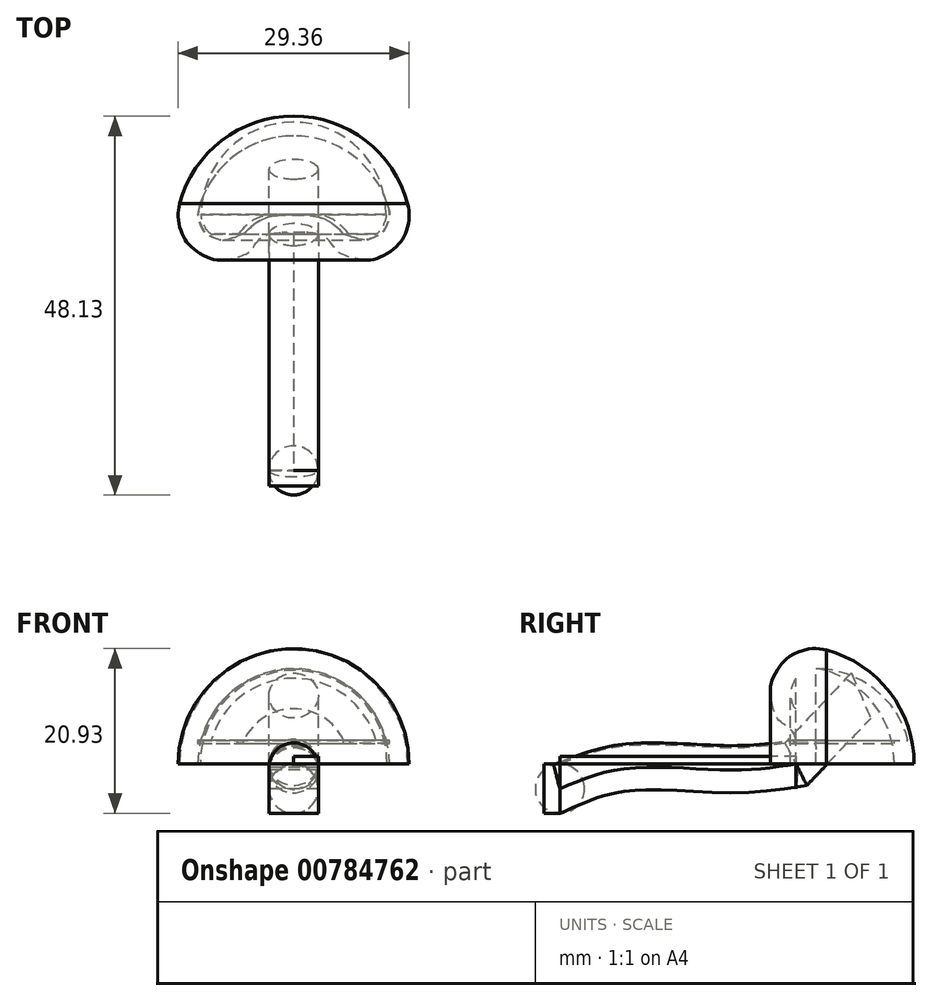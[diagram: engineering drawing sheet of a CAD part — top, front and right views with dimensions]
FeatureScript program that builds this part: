
annotation { "Feature Type Name" : "Feature", "Feature Type Description" : "" }
export const myFeature = defineFeature(function(context is Context, id is Id, definition is map)
    precondition{}
    {
        {
            var Q0;
            Q0=qCreatedBy(makeId("Top.planeOp"),FACE);
            var sketch = newSketch(context, id + "F0", { "sketchPlane" : qUnion([Q0])});
            skArc(sketch, "E0", {"start": v(14.49, 3.88) * mm, "mid": v(0, 15) * mm, "end": v(-14.49, 3.88) * mm});
            skFitSpline(sketch, "E1", {"points": [v(-14.49, 3.88) * mm, v(-14.67, 2.02) * mm, v(-14.1, -0.07) * mm, v(-13.11, -1.5) * mm, v(-10.97, -2.91) * mm, v(-8.92, -3.26) * mm, v(-6.48, -2.67) * mm, v(-5.4, -1.97) * mm, v(-4.1, -0.42) * mm, v(-2.07, 0.17) * mm, v(-1.02, 0.18) * mm, v(0, 0) * mm], "startDerivative": vector(-3.74, -19.6) * mm, "endDerivative": vector(15.18, -3.15) * mm});
            skFitSpline(sketch, "E2.MirrorCS", {"points": [v(14.49, 3.88) * mm, v(14.67, 2.02) * mm, v(14.1, -0.07) * mm, v(13.11, -1.5) * mm, v(10.97, -2.91) * mm, v(8.92, -3.26) * mm, v(6.48, -2.67) * mm, v(5.4, -1.97) * mm, v(4.1, -0.42) * mm, v(2.07, 0.17) * mm, v(1.02, 0.18) * mm, v(0, 0) * mm], "startDerivative": vector(3.74, -19.6) * mm, "endDerivative": vector(-15.18, -3.15) * mm});
            skLineSegment(sketch, "E3.trimOffspring", {"start": v(-3.13, 0) * mm, "end": v(3.13, 0) * mm});
            skLineSegment(sketch, "E4", {"start": v(0, 15) * mm, "end": v(0, 0) * mm});
            skSolve(sketch);
        }
        {
            var Q0;
            {var subQ0=sQuery(id+"F0.wireOp",EDGE,"E3.trimOffspring");var subQ1=sQuery(id+"F0.wireOp",EDGE,"E1");var subQ3=makeQuery(id+"F0.imprint","INTERSECT",VERTEX,{"derivedFrom":[subQ1,subQ0]});Q0=makeQuery(id+"F0.imprint","IMPRINT",FACE,{"disambiguationData":[TD([[makeQuery(id+"F0.imprint","IMPRINT",EDGE,{"disambiguationData":[TD([[subQ3,-1.0]])],"derivedFrom":subQ1}),-1.0]])]});}
            var Q1;
            {var subQ0=sQuery(id+"F0.wireOp",EDGE,"E3.trimOffspring");var subQ1=sQuery(id+"F0.wireOp",EDGE,"E2.MirrorCS");var subQ3=makeQuery(id+"F0.imprint","INTERSECT",VERTEX,{"derivedFrom":[subQ1,subQ0]});Q1=makeQuery(id+"F0.imprint","IMPRINT",FACE,{"disambiguationData":[TD([[makeQuery(id+"F0.imprint","IMPRINT",EDGE,{"disambiguationData":[TD([[subQ3,-1.0]])],"derivedFrom":subQ1}),1.0]])]});}
            var Q2;
            {var subQ3=sQuery(id+"F0.wireOp",EDGE,"E4");Q2=makeQuery(id+"F0.imprint","IMPRINT",FACE,{"disambiguationData":[TD([[makeQuery(id+"F0.imprint","IMPRINT",EDGE,{"derivedFrom":subQ3}),1.0]])]});}
            var Q3;
            Q3=sQuery(id+"F0.wireOp",EDGE,"E4");
            revolve(context, id + "F1", {"entities" : qUnion([Q0, Q1, Q2]), "axis" : qUnion([Q3]), "revolveType" : RevolveType.ONE_DIRECTION, "angle" : 180 * degree});
        }
        {
            var Q0;
            Q0=makeQuery(id+"F1.opRevolve","CAP_FACE",FACE,{"disambiguationData":[OSD([sQuery(id+"F0.wireOp",EDGE,"E0"),sQuery(id+"F0.wireOp",EDGE,"E2.MirrorCS"),sQuery(id+"F0.wireOp",EDGE,"E3.trimOffspring"),sQuery(id+"F0.wireOp",EDGE,"E4")])],"isStart":false});
            var sketch = newSketch(context, id + "F2", { "sketchPlane" : qUnion([Q0])});
            skArc(sketch, "E5", {"start": v(-11.88, -3.88) * mm, "mid": v(0, -12.5) * mm, "end": v(11.88, -3.88) * mm});
            skLineSegment(sketch, "E6", {"start": v(14.49, -3.88) * mm, "end": v(14.68, -2.52) * mm, "construction": true});
            skLineSegment(sketch, "E7", {"start": v(14.68, -2.52) * mm, "end": v(14.3, -0.42) * mm, "construction": true});
            skLineSegment(sketch, "E8", {"start": v(14.3, -0.42) * mm, "end": v(13.11, 1.5) * mm, "construction": true});
            skLineSegment(sketch, "E9", {"start": v(13.11, 1.5) * mm, "end": v(11.35, 2.73) * mm, "construction": true});
            skLineSegment(sketch, "E10", {"start": v(11.35, 2.73) * mm, "end": v(9.25, 3.27) * mm, "construction": true});
            skLineSegment(sketch, "E11", {"start": v(9.25, 3.27) * mm, "end": v(7.87, 3.09) * mm, "construction": true});
            skLineSegment(sketch, "E12", {"start": v(7.87, 3.09) * mm, "end": v(6.48, 2.67) * mm, "construction": true});
            skLineSegment(sketch, "E13", {"start": v(6.48, 2.67) * mm, "end": v(5.56, 2.13) * mm, "construction": true});
            skLineSegment(sketch, "E14", {"start": v(3.13, 0) * mm, "end": v(4.1, 0.43) * mm});
            skLineSegment(sketch, "E15", {"start": v(4.1, 0.43) * mm, "end": v(3.13, 0) * mm, "construction": true});
            skLineSegment(sketch, "E16", {"start": v(14.58, -3.2) * mm, "end": v(12.1, -2.86) * mm, "construction": true});
            skLineSegment(sketch, "E17", {"start": v(14.5, -1.47) * mm, "end": v(12.03, -1.9) * mm, "construction": true});
            skLineSegment(sketch, "E18", {"start": v(13.71, 0.54) * mm, "end": v(11.49, -0.6) * mm, "construction": true});
            skLineSegment(sketch, "E19", {"start": v(12.23, 2.12) * mm, "end": v(10.8, 0.07) * mm, "construction": true});
            skLineSegment(sketch, "E20", {"start": v(10.3, 3) * mm, "end": v(9.67, 0.58) * mm, "construction": true});
            skLineSegment(sketch, "E21", {"start": v(8.56, 3.18) * mm, "end": v(8.9, 0.7) * mm, "construction": true});
            skLineSegment(sketch, "E22", {"start": v(7.18, 2.88) * mm, "end": v(7.9, 0.49) * mm, "construction": true});
            skLineSegment(sketch, "E23", {"start": v(6.02, 2.4) * mm, "end": v(7.27, 0.24) * mm, "construction": true});
            skLineSegment(sketch, "E24", {"start": v(4.1, 0.43) * mm, "end": v(5.56, 2.13) * mm, "construction": true});
            skLineSegment(sketch, "E25", {"start": v(4.83, 1.28) * mm, "end": v(6.73, -0.34) * mm, "construction": true});
            skLineSegment(sketch, "E26", {"start": v(3.62, 0.22) * mm, "end": v(4.62, -2.07) * mm, "construction": true});
            skLineSegment(sketch, "E27", {"start": v(3.13, 0) * mm, "end": v(0, 0) * mm, "construction": true});
            skLineSegment(sketch, "E28", {"start": v(1.56, 0) * mm, "end": v(1.56, -2.5) * mm, "construction": true});
            skFitSpline(sketch, "E29", {"points": [v(11.88, -3.88) * mm, v(12.1, -2.86) * mm, v(12.03, -1.9) * mm, v(11.49, -0.6) * mm, v(10.8, 0.07) * mm, v(9.67, 0.58) * mm, v(8.9, 0.7) * mm, v(7.9, 0.49) * mm, v(7.27, 0.24) * mm, v(6.73, -0.34) * mm, v(4.62, -2.07) * mm, v(1.56, -2.5) * mm, v(0, -2.5) * mm], "startDerivative": vector(3.76, 13.81) * mm, "endDerivative": vector(-15.24, -0.04) * mm});
            skFitSpline(sketch, "E30.MirrorCS", {"points": [v(-11.88, -3.88) * mm, v(-12.1, -2.86) * mm, v(-12.03, -1.9) * mm, v(-11.49, -0.6) * mm, v(-10.8, 0.07) * mm, v(-9.67, 0.58) * mm, v(-8.9, 0.7) * mm, v(-7.9, 0.49) * mm, v(-7.27, 0.24) * mm, v(-6.73, -0.34) * mm, v(-4.62, -2.07) * mm, v(-1.56, -2.5) * mm, v(0, -2.5) * mm], "startDerivative": vector(-3.76, 13.81) * mm, "endDerivative": vector(15.24, -0.04) * mm});
            skLineSegment(sketch, "E31", {"start": v(0, -12.5) * mm, "end": v(0, -2.5) * mm});
            skSolve(sketch);
        }
        {
            var Q0;
            {var subQ0=sQuery(id+"F2.wireOp",EDGE,"E29");Q0=makeQuery(id+"F2.imprint","IMPRINT",FACE,{"disambiguationData":[TD([[makeQuery(id+"F2.imprint","IMPRINT",EDGE,{"derivedFrom":subQ0}),1.0]])]});}
            var Q1;
            Q1=sQuery(id+"F2.wireOp",EDGE,"E31");
            revolve(context, id + "F3", {"operationType" : NewBodyOperationType.REMOVE, "entities" : qUnion([Q0]), "axis" : qUnion([Q1]), "revolveType" : RevolveType.ONE_DIRECTION, "angle" : 180 * degree});
        }
        {
            var Q0;
            Q0=qCreatedBy(makeId("Front.planeOp"),FACE);
            var sketch = newSketch(context, id + "F4", { "sketchPlane" : qUnion([Q0])});
            skLineSegment(sketch, "E32", {"start": v(0, 0) * mm, "end": v(0, 3) * mm});
            skArc(sketch, "E33", {"start": v(14.14, 0) * mm, "mid": v(0, 14.14) * mm, "end": v(-14.14, 0) * mm});
            skLineSegment(sketch, "E34", {"start": v(0, 3) * mm, "end": v(-13.82, 3) * mm});
            skLineSegment(sketch, "E35", {"start": v(-13.82, 3) * mm, "end": v(13.82, 3) * mm});
            skLineSegment(sketch, "E36.bottom", {"start": v(-13.82, 3) * mm, "end": v(12.58, 3) * mm});
            skLineSegment(sketch, "E36.left", {"start": v(-13.82, 3) * mm, "end": v(-13.82, 3.47) * mm});
            skLineSegment(sketch, "E36.right", {"start": v(12.58, 3) * mm, "end": v(12.58, 6.47) * mm});
            skLineSegment(sketch, "E37.left", {"start": v(-13.82, 3.47) * mm, "end": v(-13.82, 3) * mm});
            skLineSegment(sketch, "E37.right", {"start": v(13.82, 3.47) * mm, "end": v(13.82, 3) * mm});
            skLineSegment(sketch, "E38.bottom", {"start": v(-0.5, 3) * mm, "end": v(1.98, 3) * mm});
            skSolve(sketch);
        }
        {
            var Q0;
            {var subQ2=sQuery(id+"F4.wireOp",EDGE,"E36.right");Q0=makeQuery(id+"F4.imprint","IMPRINT",FACE,{"disambiguationData":[TD([[makeQuery(id+"F4.imprint","IMPRINT",EDGE,{"derivedFrom":subQ2}),1.0]])]});}
            extrude(context, id + "F5", {"entities" : qUnion([Q0]), "operationType" : NewBodyOperationType.ADD, "oppositeDirection" : true, "depth" : 2.5 * mm, "offsetDistance" : 25 * mm});
        }
        {
            var Q0;
            Q0=makeQuery(id+"F5.opExtrude","CAP_FACE",FACE,{"disambiguationData":[OSD([sQuery(id+"F4.wireOp",EDGE,"E33"),sQuery(id+"F4.wireOp",EDGE,"E34"),sQuery(id+"F4.wireOp",EDGE,"E35"),sQuery(id+"F4.wireOp",EDGE,"E36.right")])],"isStart":false});
            var sketch = newSketch(context, id + "F6", { "sketchPlane" : qUnion([Q0])});
            skLineSegment(sketch, "E39", {"start": v(0, 3) * mm, "end": v(0, 12.12) * mm});
            skSolve(sketch);
        }
        {
            var Q0;
            {var subQ0=sQuery(id+"F6.wireOp",EDGE,"E39");Q0=makeQuery(id+"F6.imprint","IMPRINT",FACE,{"disambiguationData":[TD([[makeQuery(id+"F6.imprint","IMPRINT",EDGE,{"derivedFrom":subQ0}),-1.0]])]});}
            var Q1;
            Q1=sQuery(id+"F6.wireOp",EDGE,"E39");
            revolve(context, id + "F7", {"entities" : qUnion([Q0]), "axis" : qUnion([Q1]), "revolveType" : RevolveType.ONE_DIRECTION, "oppositeDirection" : true, "angle" : 180 * degree});
        }
        {
            var Q0;
            Q0=makeQuery(id+"F7.opRevolve","SWEPT_FACE",FACE,{"disambiguationData":[OSD([sQuery(id+"F4.wireOp",EDGE,"E34"),sQuery(id+"F4.wireOp",EDGE,"E35")])]});
            var sketch = newSketch(context, id + "F8", { "sketchPlane" : qUnion([Q0])});
            skArc(sketch, "E40.0", {"start": v(11.88, -3.88) * mm, "mid": v(0, -12.5) * mm, "end": v(-11.88, -3.88) * mm});
            skFitSpline(sketch, "E41.0", {"points": [v(-11.88, -3.88) * mm, v(-11.98, -3.53) * mm, v(-12.16, -2.85) * mm, v(-12.1, -1.9) * mm, v(-11.55, -0.54) * mm, v(-10.86, 0.1) * mm, v(-9.67, 0.62) * mm, v(-8.9, 0.78) * mm, v(-7.9, 0.5) * mm, v(-7.21, 0.28) * mm, v(-6.72, -0.4) * mm, v(-4.75, -2.52) * mm, v(-1.6, -2.5) * mm, v(-0.47, -2.5) * mm, v(0, -2.5) * mm]});
            skFitSpline(sketch, "E42.0", {"points": [v(11.88, -3.88) * mm, v(11.98, -3.53) * mm, v(12.16, -2.85) * mm, v(12.1, -1.9) * mm, v(11.55, -0.54) * mm, v(10.86, 0.1) * mm, v(9.67, 0.62) * mm, v(8.9, 0.78) * mm, v(7.9, 0.5) * mm, v(7.21, 0.28) * mm, v(6.72, -0.4) * mm, v(4.75, -2.52) * mm, v(1.6, -2.5) * mm, v(0.47, -2.5) * mm, v(0, -2.5) * mm]});
            skFitSpline(sketch, "E43.0", {"points": [v(-6.34, 0) * mm, v(-6.24, -0.1) * mm, v(-6.05, -0.33) * mm, v(-5.74, -0.65) * mm, v(-5.41, -0.95) * mm, v(-5.07, -1.23) * mm, v(-4.71, -1.48) * mm, v(-4.33, -1.72) * mm, v(-3.93, -1.92) * mm, v(-3.38, -2.13) * mm, v(-2.67, -2.3) * mm, v(-1.78, -2.4) * mm, v(-0.89, -2.45) * mm, v(0, -2.46) * mm, v(0.89, -2.45) * mm, v(1.78, -2.4) * mm, v(2.66, -2.3) * mm, v(3.38, -2.14) * mm, v(3.94, -1.92) * mm, v(4.46, -1.65) * mm, v(4.95, -1.33) * mm, v(5.4, -0.95) * mm, v(5.73, -0.65) * mm, v(6.04, -0.33) * mm, v(6.24, -0.1) * mm, v(6.34, 0) * mm]});
            skFitSpline(sketch, "E44.0.0", {"points": [v(0, -2.5) * mm, v(-0.47, -2.5) * mm, v(-1.6, -2.5) * mm, v(-4.75, -2.52) * mm, v(-6.72, -0.4) * mm, v(-7.21, 0.28) * mm, v(-7.9, 0.5) * mm, v(-8.9, 0.78) * mm, v(-9.67, 0.62) * mm, v(-10.86, 0.1) * mm, v(-11.55, -0.54) * mm, v(-12.1, -1.9) * mm, v(-12.16, -2.85) * mm, v(-11.98, -3.53) * mm, v(-11.88, -3.88) * mm]});
            skFitSpline(sketch, "E44.0.2", {"points": [v(11.88, -3.88) * mm, v(11.98, -3.53) * mm, v(12.16, -2.85) * mm, v(12.1, -1.9) * mm, v(11.55, -0.54) * mm, v(10.86, 0.1) * mm, v(9.67, 0.62) * mm, v(8.9, 0.78) * mm, v(7.9, 0.5) * mm, v(7.21, 0.28) * mm, v(6.72, -0.4) * mm, v(4.75, -2.52) * mm, v(1.6, -2.5) * mm, v(0.47, -2.5) * mm, v(0, -2.5) * mm]});
            skLineSegment(sketch, "E45", {"start": v(-6.34, 0) * mm, "end": v(-8.62, 0.67) * mm});
            skLineSegment(sketch, "E46", {"start": v(6.34, 0) * mm, "end": v(8.8, 0.7) * mm});
            skSolve(sketch);
        }
        {
            var Q0;
            Q0=qSketchRegion(id+"F8",true);
            extrude(context, id + "F9", {"entities" : qUnion([Q0]), "depth" : 0.4 * mm, "offsetDistance" : 25 * mm});
        }
        {
            var Q0;
            Q0=qCreatedBy(makeId("Top.planeOp"),FACE);
            var sketch = newSketch(context, id + "F10", { "sketchPlane" : qUnion([Q0])});
            skArc(sketch, "E47", {"start": v(-14.49, 3.88) * mm, "mid": v(0, 15) * mm, "end": v(14.49, 3.88) * mm, "construction": true});
            skPoint(sketch, "E48.1.internal.snap0", {"position": v(0, 15) * mm});
            skLineSegment(sketch, "E49", {"start": v(0, 15) * mm, "end": v(0, -30) * mm, "construction": true});
            skLineSegment(sketch, "E50.bottom", {"start": v(0, -30) * mm, "end": v(3.13, -30) * mm});
            skLineSegment(sketch, "E50.top", {"start": v(0, -32) * mm, "end": v(3.13, -32) * mm});
            skLineSegment(sketch, "E50.left", {"start": v(0, -30) * mm, "end": v(0, -32) * mm});
            skLineSegment(sketch, "E50.right", {"start": v(3.13, -30) * mm, "end": v(3.13, -32) * mm});
            skLineSegment(sketch, "E51.MirrorCS", {"start": v(0, -30) * mm, "end": v(-3.13, -30) * mm});
            skLineSegment(sketch, "E52.MirrorCS", {"start": v(0, -32) * mm, "end": v(-3.13, -32) * mm});
            skLineSegment(sketch, "E53.MirrorCS", {"start": v(-3.13, -30) * mm, "end": v(-3.13, -32) * mm});
            skLineSegment(sketch, "E54.bottom", {"start": v(0, 0) * mm, "end": v(3.13, 0) * mm});
            skLineSegment(sketch, "E54.left", {"start": v(0, 0) * mm, "end": v(0, -30) * mm});
            skLineSegment(sketch, "E54.right", {"start": v(3.13, 0) * mm, "end": v(3.13, -30) * mm});
            skSolve(sketch);
        }
        {
            var Q0;
            Q0=makeQuery(id+"F10.imprint","IMPRINT",FACE,{"disambiguationData":[TD([[makeQuery(id+"F10.imprint","IMPRINT",EDGE,{"derivedFrom":sQuery(id+"F10.wireOp",EDGE,"E50.left")}),-1.0]])]});
            var Q1;
            Q1=makeQuery(id+"F10.imprint","IMPRINT",FACE,{"disambiguationData":[TD([[makeQuery(id+"F10.imprint","IMPRINT",EDGE,{"derivedFrom":sQuery(id+"F10.wireOp",EDGE,"E50.top")}),1.0]])]});
            extrude(context, id + "F11", {"entities" : qUnion([Q0, Q1]), "oppositeDirection" : true, "depth" : 6.25 * mm, "offsetDistance" : 25 * mm});
        }
        {
            var Q0;
            Q0=makeQuery(id+"F11.opExtrude","SWEPT_FACE",FACE,{"disambiguationData":[OSD([sQuery(id+"F10.wireOp",EDGE,"E50.bottom"),sQuery(id+"F10.wireOp",EDGE,"E51.MirrorCS")])]});
            var sketch = newSketch(context, id + "F12", { "sketchPlane" : qUnion([Q0])});
            skLineSegment(sketch, "E55", {"start": v(-3.13, -3.13) * mm, "end": v(-3.13, 0) * mm, "construction": true});
            skLineSegment(sketch, "E56", {"start": v(3.13, -0.84) * mm, "end": v(3.13, 0) * mm, "construction": true});
            skLineSegment(sketch, "E57", {"start": v(-3.13, 0) * mm, "end": v(3.13, 0) * mm, "construction": true});
            skLineSegment(sketch, "E58", {"start": v(3.13, 0) * mm, "end": v(-3.13, -6.25) * mm, "construction": true});
            skLineSegment(sketch, "E59", {"start": v(-3.13, -6.25) * mm, "end": v(-3.13, 0) * mm});
            skLineSegment(sketch, "E60", {"start": v(3.13, -6.25) * mm, "end": v(-3.13, 0) * mm, "construction": true});
            skCircle(sketch, "E61", {"center": v(0, -3.13) * mm, "radius": 3.13 * mm});
            skSolve(sketch);
        }
        {
            var Q0;
            Q0=makeQuery(id+"F10.imprint","IMPRINT",FACE,{"disambiguationData":[TD([[makeQuery(id+"F10.imprint","IMPRINT",EDGE,{"derivedFrom":sQuery(id+"F10.wireOp",EDGE,"E54.bottom")}),-1.0]])]});
            extrude(context, id + "F13", {"entities" : qUnion([Q0]), "depth" : 1 * mm, "offsetDistance" : 25 * mm});
        }
        {
            var Q0;
            Q0=makeQuery(id+"F13.opExtrude","SWEPT_FACE",FACE,{"disambiguationData":[OSD([sQuery(id+"F10.wireOp",EDGE,"E54.left")])]});
            var sketch = newSketch(context, id + "F14", { "sketchPlane" : qUnion([Q0])});
            skLineSegment(sketch, "E62.0.0", {"start": v(32, 0) * mm, "end": v(30, 0) * mm, "construction": true});
            skLineSegment(sketch, "E62.0.1", {"start": v(30, 0) * mm, "end": v(30, -6.25) * mm, "construction": true});
            skLineSegment(sketch, "E62.0.2", {"start": v(30, -6.25) * mm, "end": v(32, -6.25) * mm, "construction": true});
            skLineSegment(sketch, "E62.0.3", {"start": v(32, -6.25) * mm, "end": v(32, 0) * mm, "construction": true});
            skFitSpline(sketch, "E63", {"points": [v(30, -3.13) * mm, v(21.56, -0.56) * mm, v(8.18, -0.75) * mm, v(0, 0) * mm], "startDerivative": vector(-24.58, 10.5) * mm, "endDerivative": vector(-24.77, 3.75) * mm});
            skLineSegment(sketch, "E64", {"start": v(0, 0) * mm, "end": v(-8.26, 8.7) * mm});
            skSolve(sketch);
        }
        {
            var Q0;
            {var subQ0=sQuery(id+"F12.wireOp",EDGE,"E61");var subQ5=makeQuery(id+"F12.imprint","INTERSECT",VERTEX,{"derivedFrom":[sQuery(id+"F12.wireOp",EDGE,"E59"),subQ0]});Q0=makeQuery(id+"F12.imprint","IMPRINT",FACE,{"disambiguationData":[TD([[makeQuery(id+"F12.imprint","IMPRINT",EDGE,{"disambiguationData":[TD([[subQ5,1.0]])],"derivedFrom":subQ0}),1.0]])]});}
            var Q1;
            Q1=sQuery(id+"F14.wireOp",EDGE,"E63");
            var Q2;
            Q2=sQuery(id+"F14.wireOp",EDGE,"E64");
            sweep(context, id + "F15", {"profiles" : qUnion([Q0]), "path" : qUnion([Q1, Q2])});
        }
        {
            var Q0;
            {var subQ0=sQuery(id+"F0.wireOp",EDGE,"E3.trimOffspring");var subQ1=sQuery(id+"F0.wireOp",EDGE,"E2.MirrorCS");Q0=makeQuery(id+"F1.opRevolve","SWEPT_FACE",FACE,{"disambiguationData":[OSD([subQ0]),TDD([makeQuery(id+"F0.imprint","IMPRINT",EDGE,{"disambiguationData":[TD([[makeQuery(id+"F0.imprint","INTERSECT",VERTEX,{"derivedFrom":[subQ1,subQ0]}),1.0]])],"derivedFrom":subQ0})])]});}
            var Q1;
            Q1=sQuery(id+"F14.wireOp",EDGE,"E63");
            var Q2;
            Q2=sQuery(id+"F14.wireOp",EDGE,"YPlXaDKz-pfN4-AJQ7-obvI-QgIjoEGbB2oJ");
            sweep(context, id + "F16", {"profiles" : qUnion([Q0]), "path" : qUnion([Q1, Q2])});
        }
        {
            var Q0;
            Q0=makeQuery(id+"F16.opSweep","CAP_FACE",FACE,{"disambiguationData":[OSD([sQuery(id+"F0.wireOp",EDGE,"E3.trimOffspring"),sQuery(id+"F14.wireOp",VERTEX,"E63.start")])],"isStart":false});
            var Q1;
            Q1=makeQuery(id+"F16.opSweep","CAP_EDGE",EDGE,{"disambiguationData":[OSD([sQuery(id+"F0.wireOp",EDGE,"E3.trimOffspring"),sQuery(id+"F14.wireOp",VERTEX,"E63.start")])],"isStart":false});
            revolve(context, id + "F17", {"entities" : qUnion([Q0]), "axis" : qUnion([Q1]), "revolveType" : RevolveType.FULL});
        }
    });
